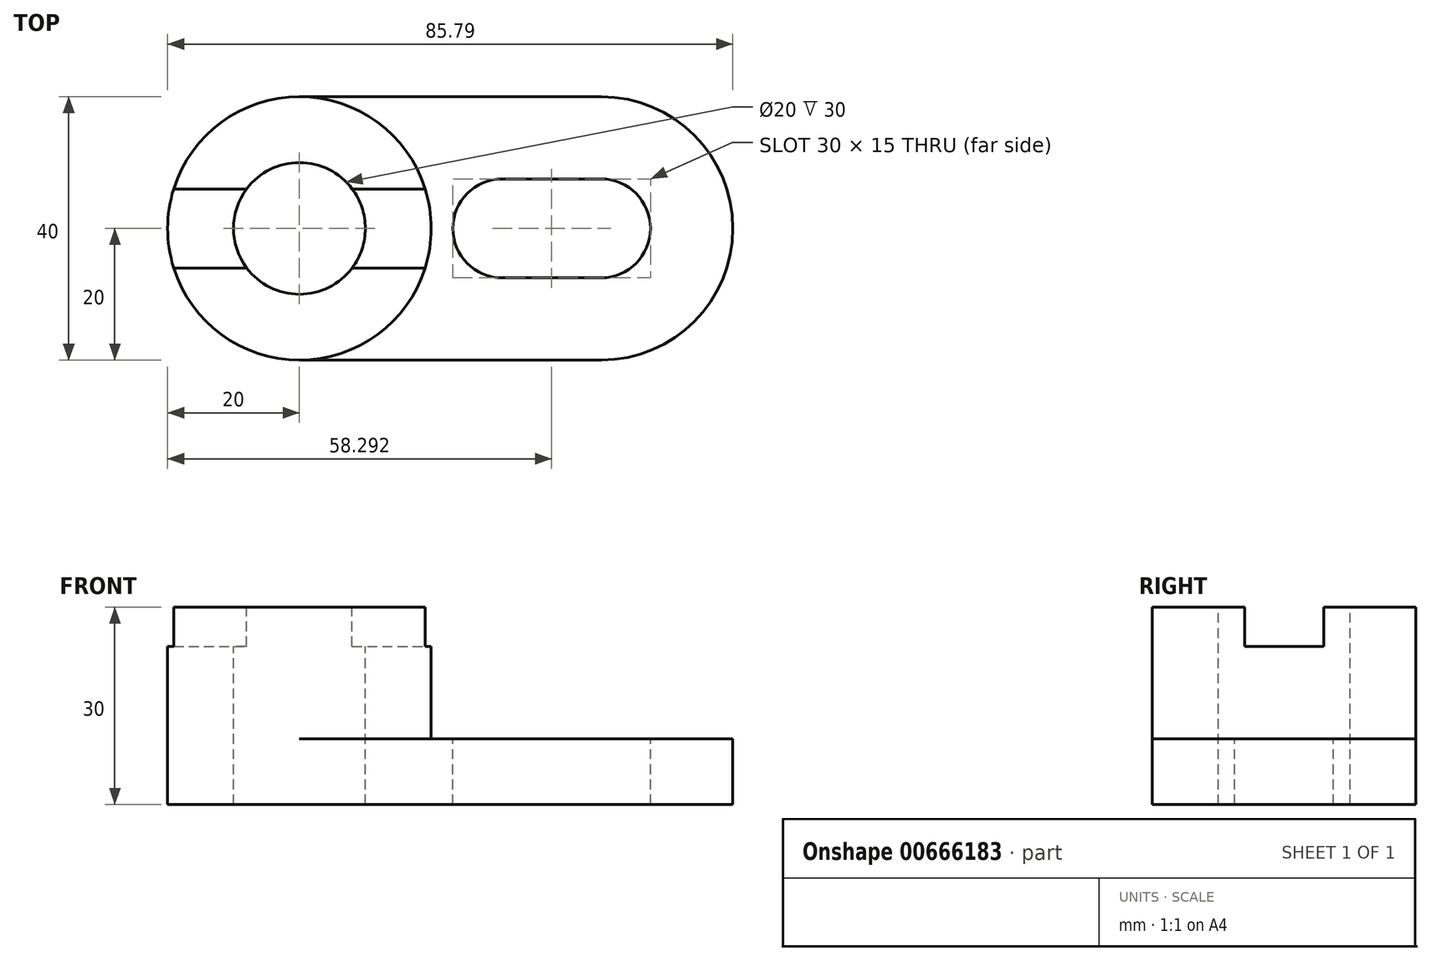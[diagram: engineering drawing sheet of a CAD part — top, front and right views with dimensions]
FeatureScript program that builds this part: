
annotation { "Feature Type Name" : "Feature", "Feature Type Description" : "" }
export const myFeature = defineFeature(function(context is Context, id is Id, definition is map)
    precondition{}
    {
        {
            var Q0;
            Q0=qCreatedBy(makeId("Top.planeOp"),FACE);
            var sketch = newSketch(context, id + "F0", { "sketchPlane" : qUnion([Q0])});
            skArc(sketch, "E0", {"start": v(0, 20) * mm, "mid": v(-20, 0) * mm, "end": v(0, -20) * mm});
            skArc(sketch, "E1", {"start": v(45.8, -20) * mm, "mid": v(65.8, 0) * mm, "end": v(45.8, 20) * mm});
            skLineSegment(sketch, "E2", {"start": v(0, 20) * mm, "end": v(45.8, 20) * mm});
            skLineSegment(sketch, "E3", {"start": v(0, -20) * mm, "end": v(45.8, -20) * mm});
            skSolve(sketch);
        }
        {
            var Q0;
            Q0 = qSketchRegion(id + "F0", true);
            extrude(context, id + "F1", {"entities" : qUnion([Q0]), "depth" : 10 * mm, "offsetDistance" : 25 * mm});
        }
        {
            var Q0;
            Q0=makeQuery(id+"F1.opExtrude","CAP_FACE",FACE,{"disambiguationData":[OSD([sQuery(id+"F0.wireOp",EDGE,"E0"),sQuery(id+"F0.wireOp",EDGE,"E1"),sQuery(id+"F0.wireOp",EDGE,"E2"),sQuery(id+"F0.wireOp",EDGE,"E3")])],"isStart":false});
            var sketch = newSketch(context, id + "F2", { "sketchPlane" : qUnion([Q0])});
            skCircle(sketch, "E4", {"center": v(0, 0) * mm, "radius": 20 * mm});
            skSolve(sketch);
        }
        {
            var Q0;
            Q0 = qSketchRegion(id + "F2", true);
            extrude(context, id + "F3", {"entities" : qUnion([Q0]), "operationType" : NewBodyOperationType.ADD, "depth" : 20 * mm, "offsetDistance" : 25 * mm});
        }
        {
            var Q0;
            Q0=makeQuery(id+"F3.opExtrude","CAP_FACE",FACE,{"disambiguationData":[OSD([sQuery(id+"F2.wireOp",EDGE,"E4")])],"isStart":false});
            var sketch = newSketch(context, id + "F4", { "sketchPlane" : qUnion([Q0])});
            skCircle(sketch, "E5", {"center": v(0, 0) * mm, "radius": 10 * mm});
            skSolve(sketch);
        }
        {
            var Q0;
            Q0 = qSketchRegion(id + "F4", true);
            extrude(context, id + "F5", {"entities" : qUnion([Q0]), "operationType" : NewBodyOperationType.REMOVE, "oppositeDirection" : true, "depth" : 58.8 * mm, "offsetDistance" : 25 * mm});
        }
        {
            var Q0;
            Q0=makeQuery(id+"F3.opExtrude","CAP_FACE",FACE,{"disambiguationData":[OSD([sQuery(id+"F2.wireOp",EDGE,"E4")])],"isStart":false});
            var sketch = newSketch(context, id + "F6", { "sketchPlane" : qUnion([Q0])});
            skLineSegment(sketch, "E6.bottom", {"start": v(-25, 6) * mm, "end": v(25, 6) * mm});
            skLineSegment(sketch, "E6.top", {"start": v(-25, -6) * mm, "end": v(25, -6) * mm});
            skLineSegment(sketch, "E6.left", {"start": v(-25, 6) * mm, "end": v(-25, -6) * mm});
            skLineSegment(sketch, "E6.right", {"start": v(25, 6) * mm, "end": v(25, -6) * mm});
            skSolve(sketch);
        }
        {
            var Q0;
            Q0 = qSketchRegion(id + "F6", true);
            extrude(context, id + "F7", {"entities" : qUnion([Q0]), "operationType" : NewBodyOperationType.REMOVE, "oppositeDirection" : true, "depth" : 6 * mm, "offsetDistance" : 25 * mm});
        }
        {
            var Q0;
            Q0=makeQuery(id+"F1.opExtrude","CAP_FACE",FACE,{"disambiguationData":[OSD([sQuery(id+"F0.wireOp",EDGE,"E0"),sQuery(id+"F0.wireOp",EDGE,"E1"),sQuery(id+"F0.wireOp",EDGE,"E2"),sQuery(id+"F0.wireOp",EDGE,"E3")])],"isStart":false});
            var sketch = newSketch(context, id + "F8", { "sketchPlane" : qUnion([Q0])});
            skArc(sketch, "E7", {"start": v(30.8, 7.5) * mm, "mid": v(23.3, 0) * mm, "end": v(30.8, -7.5) * mm});
            skArc(sketch, "E8", {"start": v(45.8, -7.5) * mm, "mid": v(53.3, 0) * mm, "end": v(45.8, 7.5) * mm});
            skLineSegment(sketch, "E9", {"start": v(30.8, 7.5) * mm, "end": v(45.8, 7.5) * mm});
            skLineSegment(sketch, "E10", {"start": v(30.8, -7.5) * mm, "end": v(45.8, -7.5) * mm});
            skSolve(sketch);
        }
        {
            var Q0;
            Q0=makeQuery(id+"F8.imprint","IMPRINT",FACE,{"disambiguationData":[TD([[makeQuery(id+"F8.imprint","IMPRINT",EDGE,{"derivedFrom":sQuery(id+"F8.wireOp",EDGE,"E7")}),1.0]])]});
            extrude(context, id + "F9", {"entities" : qUnion([Q0]), "operationType" : NewBodyOperationType.REMOVE, "oppositeDirection" : true, "depth" : 10 * mm, "offsetDistance" : 25 * mm});
        }
    });
